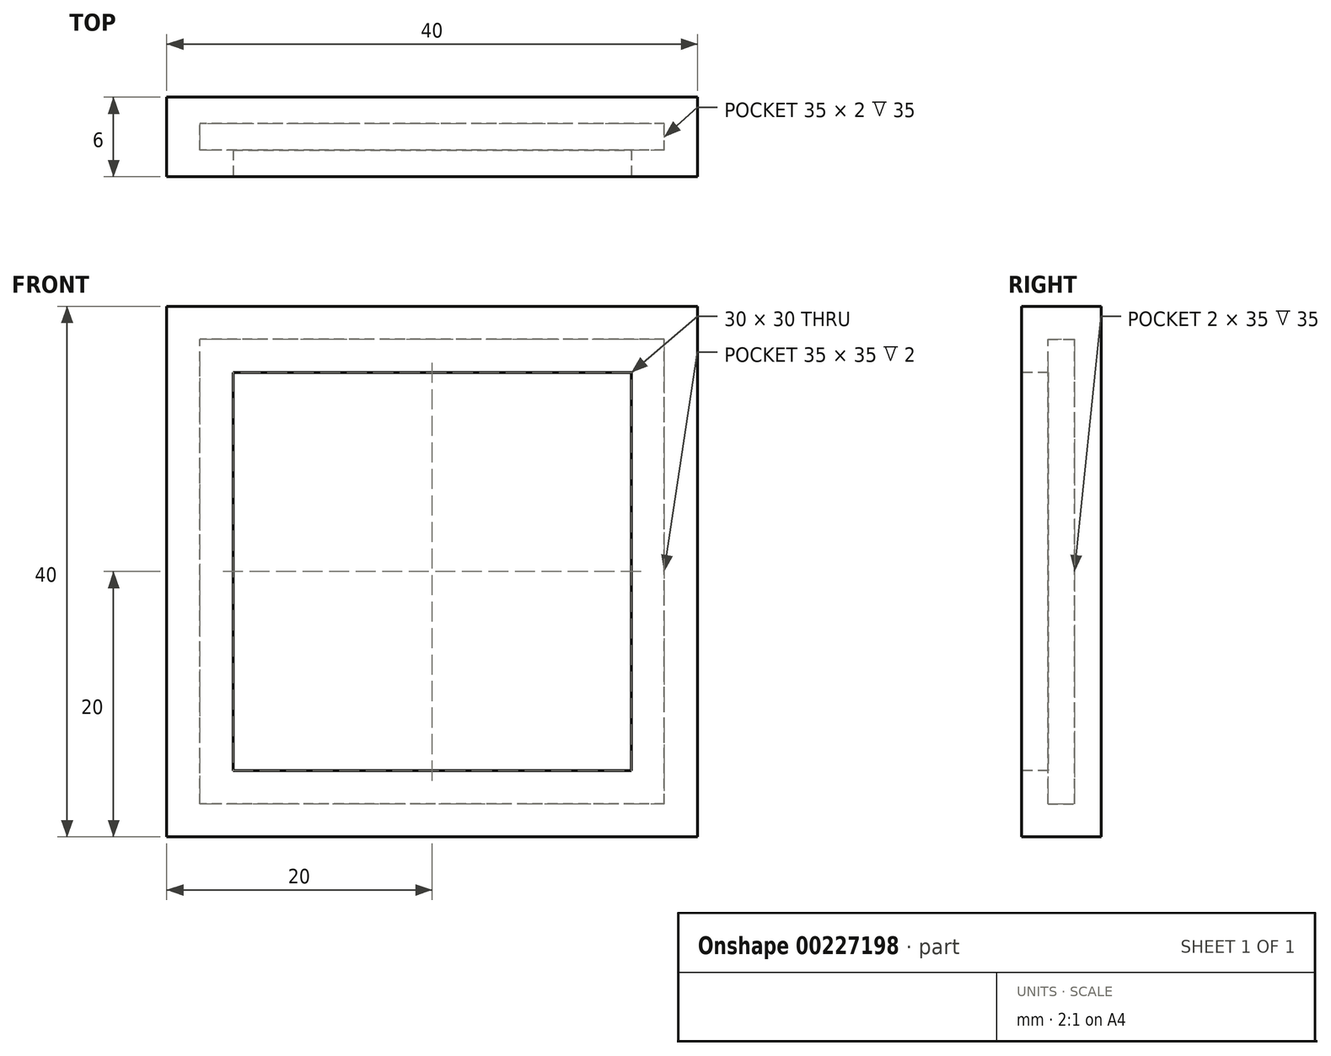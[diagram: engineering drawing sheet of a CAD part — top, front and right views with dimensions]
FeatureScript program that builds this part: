
annotation { "Feature Type Name" : "Feature", "Feature Type Description" : "" }
export const myFeature = defineFeature(function(context is Context, id is Id, definition is map)
    precondition{}
    {
        {
            var Q0;
            Q0=qCreatedBy(makeId("Front.planeOp"),FACE);
            var sketch = newSketch(context, id + "F0", { "sketchPlane" : qUnion([Q0])});
            skLineSegment(sketch, "E0.bottom", {"start": v(20, -20) * mm, "end": v(-20, -20) * mm});
            skLineSegment(sketch, "E0.top", {"start": v(20, 20) * mm, "end": v(-20, 20) * mm});
            skLineSegment(sketch, "E0.left", {"start": v(20, -20) * mm, "end": v(20, 20) * mm});
            skLineSegment(sketch, "E0.right", {"start": v(-20, -20) * mm, "end": v(-20, 20) * mm});
            skPoint(sketch, "E0.middle", {"position": v(0, 0) * mm});
            skLineSegment(sketch, "E1.bottom", {"start": v(17.5, -17.5) * mm, "end": v(-17.5, -17.5) * mm});
            skLineSegment(sketch, "E1.top", {"start": v(17.5, 17.5) * mm, "end": v(-17.5, 17.5) * mm});
            skLineSegment(sketch, "E1.left", {"start": v(17.5, -17.5) * mm, "end": v(17.5, 17.5) * mm});
            skLineSegment(sketch, "E1.right", {"start": v(-17.5, -17.5) * mm, "end": v(-17.5, 17.5) * mm});
            skSolve(sketch);
        }
        {
            var Q0;
            Q0 = qSketchRegion(id + "F0", true);
            extrude(context, id + "F1", {"entities" : qUnion([Q0]), "depth" : 6 * mm});
        }
        {
            var Q0;
            Q0=makeQuery(id+"F0.imprint","IMPRINT",FACE,{"disambiguationData":[TD([[makeQuery(id+"F0.imprint","IMPRINT",EDGE,{"derivedFrom":sQuery(id+"F0.wireOp",EDGE,"E1.bottom")}),-1.0]])]});
            extrude(context, id + "F2", {"entities" : qUnion([Q0]), "operationType" : NewBodyOperationType.ADD, "depth" : 2 * mm});
        }
        {
            var Q0;
            Q0=makeQuery(id+"F1.opExtrude","CAP_FACE",FACE,{"disambiguationData":[OSD([sQuery(id+"F0.wireOp",EDGE,"E0.bottom"),sQuery(id+"F0.wireOp",EDGE,"E0.top"),sQuery(id+"F0.wireOp",EDGE,"E0.left"),sQuery(id+"F0.wireOp",EDGE,"E0.right"),sQuery(id+"F0.wireOp",EDGE,"E1.bottom"),sQuery(id+"F0.wireOp",EDGE,"E1.top"),sQuery(id+"F0.wireOp",EDGE,"E1.left"),sQuery(id+"F0.wireOp",EDGE,"E1.right")])],"isStart":false});
            var sketch = newSketch(context, id + "F3", { "sketchPlane" : qUnion([Q0])});
            skLineSegment(sketch, "E2", {"start": v(-17.5, 15) * mm, "end": v(17.5, 15) * mm});
            skLineSegment(sketch, "E3", {"start": v(15, 15) * mm, "end": v(15, -20) * mm});
            skLineSegment(sketch, "E4", {"start": v(15, -15) * mm, "end": v(-20, -15) * mm});
            skLineSegment(sketch, "E5", {"start": v(-15, -15) * mm, "end": v(-15, 15) * mm});
            skSolve(sketch);
        }
        {
            var Q0;
            {var subQ0=makeQuery(id+"F1.opExtrude","CAP_EDGE",EDGE,{"disambiguationData":[OSD([sQuery(id+"F0.wireOp",EDGE,"E1.top")])],"isStart":false});Q0=makeQuery(id+"F3.imprint","IMPRINT",FACE,{"disambiguationData":[TD([[makeQuery(id+"F3.imprint","IMPRINT",EDGE,{"derivedFrom":subQ0}),1.0]])]});}
            var Q1;
            {var subQ3=sQuery(id+"F3.wireOp",EDGE,"E5");Q1=makeQuery(id+"F3.imprint","IMPRINT",FACE,{"disambiguationData":[TD([[makeQuery(id+"F3.imprint","IMPRINT",EDGE,{"derivedFrom":subQ3}),1.0]])]});}
            var Q2;
            {var subQ3=sQuery(id+"F3.wireOp",EDGE,"E3");var subQ5=sQuery(id+"F3.wireOp",EDGE,"E4");var subQ8=makeQuery(id+"F3.imprint","INTERSECT",VERTEX,{"derivedFrom":[subQ3,subQ5]});Q2=makeQuery(id+"F3.imprint","IMPRINT",FACE,{"disambiguationData":[TD([[makeQuery(id+"F3.imprint","IMPRINT",EDGE,{"disambiguationData":[TD([[subQ8,-1.0]])],"derivedFrom":subQ3}),-1.0]])]});}
            var Q3;
            {var subQ4=sQuery(id+"F3.wireOp",EDGE,"E2");var subQ6=makeQuery(id+"F1.opExtrude","CAP_EDGE",EDGE,{"disambiguationData":[OSD([sQuery(id+"F0.wireOp",EDGE,"E1.left")])],"isStart":false});var subQ8=makeQuery(id+"F3.imprint","INTERSECT",VERTEX,{"derivedFrom":[subQ6,subQ4]});Q3=makeQuery(id+"F3.imprint","IMPRINT",FACE,{"disambiguationData":[TD([[makeQuery(id+"F3.imprint","IMPRINT",EDGE,{"disambiguationData":[TD([[subQ8,1.0]])],"derivedFrom":subQ4}),-1.0]])]});}
            extrude(context, id + "F4", {"entities" : qUnion([Q0, Q1, Q2, Q3]), "operationType" : NewBodyOperationType.ADD, "oppositeDirection" : true, "depth" : 2 * mm});
        }
    });
